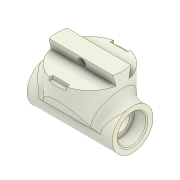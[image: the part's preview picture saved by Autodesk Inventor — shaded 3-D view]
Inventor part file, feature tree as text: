
AUTODESK INVENTOR PART (.ipt)
format: ipt  version: 2022 (Build 260153000, 153)  size: 372,224 bytes
history: native  units: mm
features: sketch x13, extrude x8, hole x5, projected_geometry x5, mirror x3, chamfer x2, plane x2, thicken_offset x1, fillet x1, split x1
ambient origin geometry x8: Origin, YZ Plane, XZ Plane, XY Plane, X Axis, Y Axis, Z Axis, Center Point
bodies: Solid1 (feature_tree), Solid2 (feature_tree), Solid3 (feature_tree)
feature tree (41):
  extrude  "Extrusion1"  Depth=5.0mm TaperAngle=0.0deg
  extrude  "Extrusion2"  Depth=40.0mm TaperAngle=0.0deg
  sketch  "Sketch4"  dims[d9=6.0mm d10=4.0mm d11=2.0mm d12=90.0deg d13=6.0mm d14=0.0mm d15=24.0mm]
  hole  "Hole1"  [1 undecoded]
  mirror  "Mirror1"
  hole  "Hole5"  [1 undecoded]
  thicken_offset  "Thicken1"
  extrude  "Extrusion3"  Depth=5.0mm
  extrude  "Extrusion4"  Depth=4.0mm TaperAngle=45.0deg
  fillet  "Fillet1"  Radius=0.2mm
  hole  "Hole2"  [1 undecoded]
  hole  "Hole3"  [1 undecoded]
  chamfer  "Chamfer1"  [1 undecoded]
  chamfer  "Chamfer2"  Distance=15.5mm
  plane  "Work Plane1"
  split  "Split1"
  extrude  "Extrusion8"  Depth=8.0mm
  extrude  "Extrusion10"  Depth=8.0mm
  plane  "Work Plane5"
  hole  "Hole9"  [1 undecoded]
  extrude  "Extrusion11"  Depth=8.0mm
  mirror  "Mirror2"
  extrude  "Extrusion12"  TaperAngle=0.0deg  [1 undecoded]
  mirror  "Mirror3"
  sketch  "Sketch1"  dims[d1=5.0mm d2=25.75mm d3=0.0mm]
  sketch  "Sketch2"  dims[d5=3.0mm d6=40.0mm d7=0.0mm]
  sketch  "Sketch3"  dims[d8=13.0mm]
  sketch  "Sketch5"  dims[d16=5.0mm d17=0.0mm d18=0.0mm d19=0.0mm]
  sketch  "Sketch6"  dims[d20=5.0mm d21=15.0mm]
  sketch  "Sketch7"  dims[d22=40.0mm d24=360.0deg]
  sketch  "Sketch9"  dims[d26=2.0mm d27=6.0mm d28=4.0mm d29=2.0mm d30=90.0deg d31=5.0mm d32=20.594885mm]
  sketch  "Sketch21"  dims[d33=10.0mm d34=6.0mm d35=4.0mm d36=2.0mm d37=90.0deg d38=2.0mm d39=0.0mm d40=2.0mm d41=2.0mm d42=45.0deg d50=0.2mm d51=0.15mm]
  sketch  "Sketch23"  dims[d52=9.0mm d53=6.0mm d54=4.0mm d55=2.0mm d56=90.0deg d57=6.0mm d58=0.0mm d59=0.5mm d60=2.0mm d61=45.0deg]
  sketch  "Sketch24"  dims[d62=-7.0mm d105=5.0mm d106=0.0mm]
  projected_geometry  "Projected Loop2"
  sketch  "Sketch25"  dims[d110=9.0mm]
  sketch  "Sketch26"  dims[d112=6.5mm d113=0.0mm d114=0.0mm d115=15.5mm d116=3.4mm d117=6.0mm d118=4.0mm d119=2.0mm d120=90.0deg d121=8.0mm d122=20.594885mm d123=8.0mm d124=8.0mm d125=2.0mm d126=0.0mm d127=0.2mm d128=0.0mm d129=0.0mm d43=0.15mm d44=0.25mm d45=0.375mm d46=14.3117mm d47=0.75mm d48=20.594885mm d49=0.0625mm]
  projected_geometry  "Project Cut Edges1"
  projected_geometry  "Project Cut Edges2"
  projected_geometry  "Project Cut Edges3"
  projected_geometry  "Project Cut Edges4"
note: 7 required parameter values undecoded (feature->parameter linkage not recoverable at this tier; creation-order binding heuristic only, values carry confidence <= 0.55)
